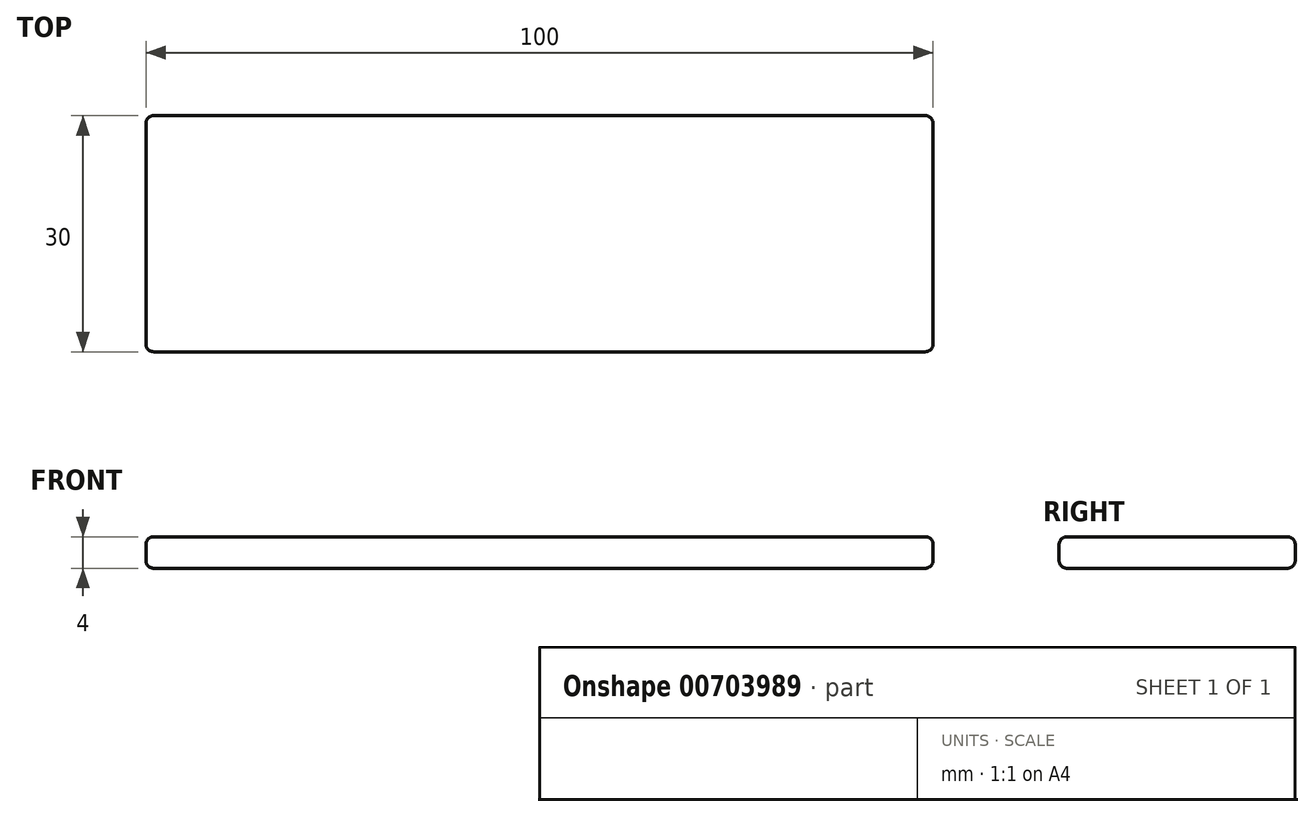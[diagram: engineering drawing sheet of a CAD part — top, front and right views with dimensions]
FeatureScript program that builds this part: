
annotation { "Feature Type Name" : "Feature", "Feature Type Description" : "" }
export const myFeature = defineFeature(function(context is Context, id is Id, definition is map)
    precondition{}
    {
        {
            var Q0;
            Q0=qCreatedBy(makeId("Top.planeOp"),FACE);
            var sketch = newSketch(context, id + "F0", { "sketchPlane" : qUnion([Q0])});
            skLineSegment(sketch, "E0.bottom", {"start": v(50, 15) * mm, "end": v(-50, 15) * mm});
            skLineSegment(sketch, "E0.top", {"start": v(50, -15) * mm, "end": v(-50, -15) * mm});
            skLineSegment(sketch, "E0.left", {"start": v(50, 15) * mm, "end": v(50, -15) * mm});
            skLineSegment(sketch, "E0.right", {"start": v(-50, 15) * mm, "end": v(-50, -15) * mm});
            skPoint(sketch, "E0.middle", {"position": v(0, 0) * mm});
            skSolve(sketch);
        }
        {
            var Q0;
            Q0=makeQuery(id+"F0.imprint","IMPRINT",FACE,{"disambiguationData":[TD([[makeQuery(id+"F0.imprint","IMPRINT",EDGE,{"derivedFrom":sQuery(id+"F0.wireOp",EDGE,"E0.bottom")}),1.0]])]});
            extrude(context, id + "F1", {"entities" : qUnion([Q0]), "oppositeDirection" : true, "depth" : 4 * mm, "offsetDistance" : 25 * mm});
        }
        {
            var Q0;
            Q0=makeQuery(id+"F1.opExtrude","CAP_EDGE",EDGE,{"disambiguationData":[OSD([sQuery(id+"F0.wireOp",EDGE,"E0.bottom")])],"isStart":true});
            var Q1;
            Q1=makeQuery(id+"F1.opExtrude","CAP_EDGE",EDGE,{"disambiguationData":[OSD([sQuery(id+"F0.wireOp",EDGE,"E0.bottom")])],"isStart":false});
            var Q2;
            Q2=makeQuery(id+"F1.opExtrude","CAP_EDGE",EDGE,{"disambiguationData":[OSD([sQuery(id+"F0.wireOp",EDGE,"E0.right")])],"isStart":true});
            var Q3;
            Q3=makeQuery(id+"F1.opExtrude","CAP_EDGE",EDGE,{"disambiguationData":[OSD([sQuery(id+"F0.wireOp",EDGE,"E0.right")])],"isStart":false});
            var Q4;
            Q4=makeQuery(id+"F1.opExtrude","SWEPT_EDGE",EDGE,{"disambiguationData":[OSD([sQuery(id+"F0.wireOp",EDGE,"E0.bottom"),sQuery(id+"F0.wireOp",EDGE,"E0.right")])]});
            var Q5;
            Q5=makeQuery(id+"F1.opExtrude","SWEPT_EDGE",EDGE,{"disambiguationData":[OSD([sQuery(id+"F0.wireOp",EDGE,"E0.bottom"),sQuery(id+"F0.wireOp",EDGE,"E0.left")])]});
            var Q6;
            Q6=makeQuery(id+"F1.opExtrude","CAP_EDGE",EDGE,{"disambiguationData":[OSD([sQuery(id+"F0.wireOp",EDGE,"E0.left")])],"isStart":false});
            var Q7;
            Q7=makeQuery(id+"F1.opExtrude","CAP_EDGE",EDGE,{"disambiguationData":[OSD([sQuery(id+"F0.wireOp",EDGE,"E0.left")])],"isStart":true});
            var Q8;
            Q8=makeQuery(id+"F1.opExtrude","SWEPT_EDGE",EDGE,{"disambiguationData":[OSD([sQuery(id+"F0.wireOp",EDGE,"E0.top"),sQuery(id+"F0.wireOp",EDGE,"E0.left")])]});
            var Q9;
            Q9=makeQuery(id+"F1.opExtrude","CAP_EDGE",EDGE,{"disambiguationData":[OSD([sQuery(id+"F0.wireOp",EDGE,"E0.top")])],"isStart":false});
            var Q10;
            Q10=makeQuery(id+"F1.opExtrude","CAP_EDGE",EDGE,{"disambiguationData":[OSD([sQuery(id+"F0.wireOp",EDGE,"E0.top")])],"isStart":true});
            var Q11;
            Q11=makeQuery(id+"F1.opExtrude","SWEPT_EDGE",EDGE,{"disambiguationData":[OSD([sQuery(id+"F0.wireOp",EDGE,"E0.top"),sQuery(id+"F0.wireOp",EDGE,"E0.right")])]});
            fillet(context, id + "F2", {"entities" : qUnion([Q0, Q1, Q2, Q3, Q4, Q5, Q6, Q7, Q8, Q9, Q10, Q11]), "radius" : 1 * mm, "tangentPropagation" : true, "allowEdgeOverflow" : false});
        }
    });
